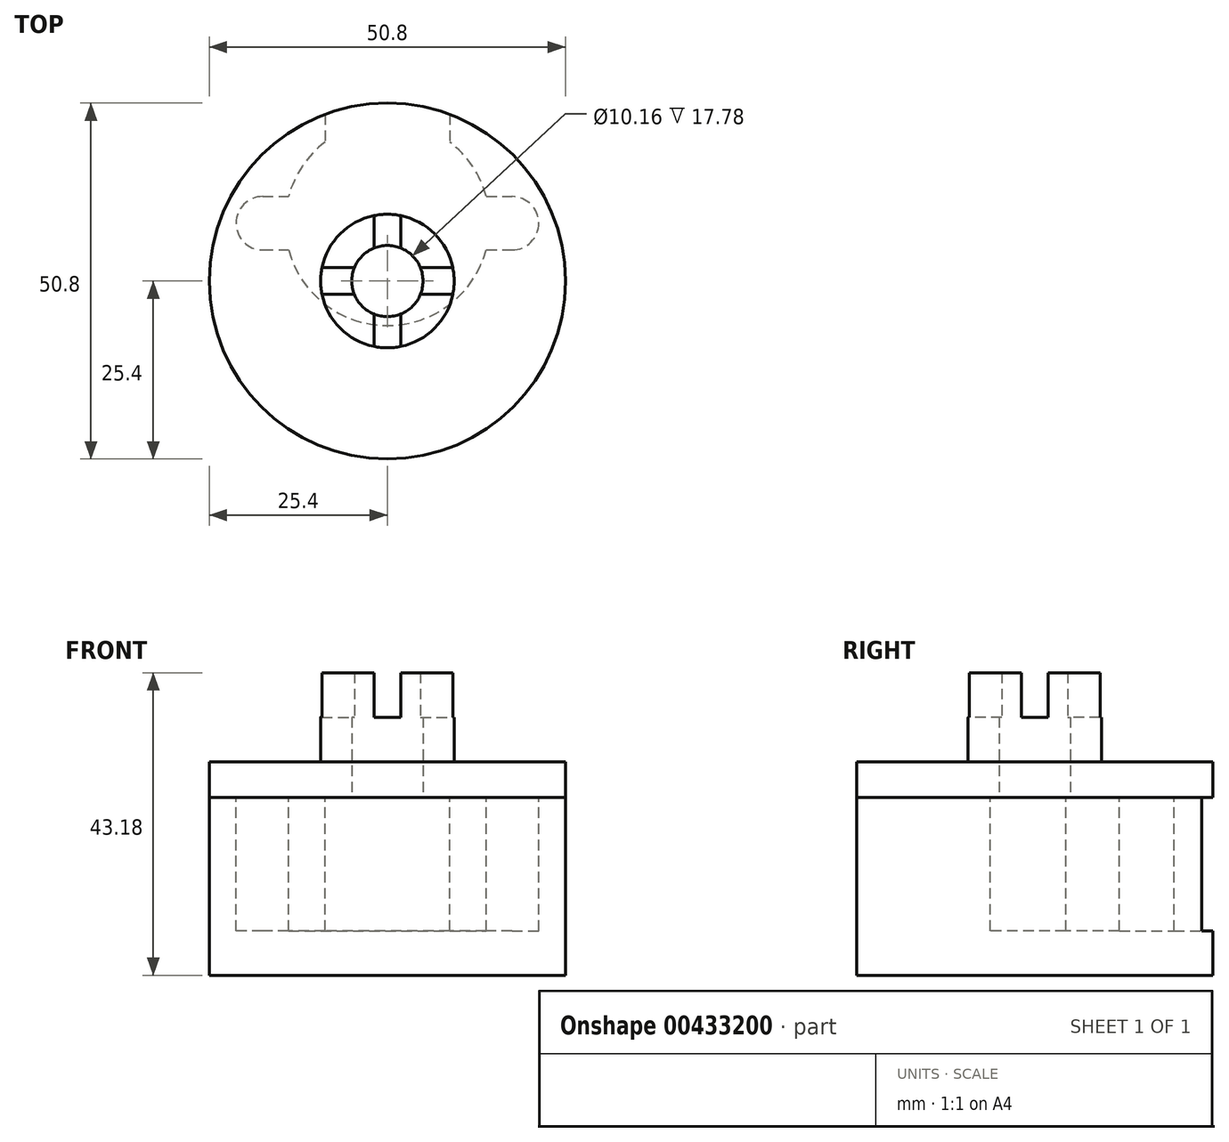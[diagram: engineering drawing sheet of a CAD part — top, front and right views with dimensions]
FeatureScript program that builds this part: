
annotation { "Feature Type Name" : "Feature", "Feature Type Description" : "" }
export const myFeature = defineFeature(function(context is Context, id is Id, definition is map)
    precondition{}
    {
        {
            var Q0;
            Q0=qCreatedBy(makeId("Top.planeOp"),FACE);
            var sketch = newSketch(context, id + "F0", { "sketchPlane" : qUnion([Q0])});
            skCircle(sketch, "E0", {"center": v(0, 0) * mm, "radius": 25.4 * mm});
            skSolve(sketch);
        }
        {
            var Q0;
            Q0=qSketchRegion(id+"F0",true);
            extrude(context, id + "F1", {"entities" : qUnion([Q0]), "depth" : 25.4 * mm});
        }
        {
            var Q0;
            Q0=makeQuery(id+"F1.opExtrude","CAP_FACE",FACE,{"disambiguationData":[OSD([sQuery(id+"F0.wireOp",EDGE,"E0")])],"isStart":false});
            var sketch = newSketch(context, id + "F2", { "sketchPlane" : qUnion([Q0])});
            skCircle(sketch, "E1", {"center": v(0, 8.26) * mm, "radius": 14.6 * mm});
            skSolve(sketch);
        }
        {
            var Q0;
            Q0=qSketchRegion(id+"F2",true);
            extrude(context, id + "F3", {"entities" : qUnion([Q0]), "operationType" : NewBodyOperationType.REMOVE, "oppositeDirection" : true, "depth" : 19.05 * mm});
        }
        {
            var Q0;
            Q0=qCreatedBy(makeId("Front.planeOp"),FACE);
            var sketch = newSketch(context, id + "F4", { "sketchPlane" : qUnion([Q0])});
            skLineSegment(sketch, "E2.bottom", {"start": v(3.81, 25.4) * mm, "end": v(-3.81, 25.4) * mm});
            skLineSegment(sketch, "E2.top", {"start": v(3.81, 21.6) * mm, "end": v(-3.81, 21.6) * mm});
            skLineSegment(sketch, "E2.left", {"start": v(3.8, 25.4) * mm, "end": v(3.8, 21.6) * mm});
            skLineSegment(sketch, "E2.right", {"start": v(-3.81, 25.4) * mm, "end": v(-3.81, 21.6) * mm});
            skPoint(sketch, "E3", {"position": v(0, 21.6) * mm});
            skPoint(sketch, "E4", {"position": v(0, 0) * mm});
            skSolve(sketch);
        }
        {
            var Q0;
            Q0=qSketchRegion(id+"F4",true);
            extrude(context, id + "F5", {"entities" : qUnion([Q0]), "operationType" : NewBodyOperationType.REMOVE, "endBound" : BoundingType.THROUGH_ALL, "oppositeDirection" : true, "depth" : 25.4 * mm});
        }
        {
            var Q0;
            Q0=makeQuery(id+"F1.opExtrude","CAP_FACE",FACE,{"disambiguationData":[OSD([sQuery(id+"F0.wireOp",EDGE,"E0")])],"isStart":true});
            var sketch = newSketch(context, id + "F6", { "sketchPlane" : qUnion([Q0])});
            skCircle(sketch, "E5", {"center": v(0, 0) * mm, "radius": 26.67 * mm});
            skCircle(sketch, "E6", {"center": v(0, 0) * mm, "radius": 39.37 * mm});
            skSolve(sketch);
        }
        {
            var Q0;
            {var subQ0=sQuery(id+"F0.wireOp",EDGE,"E0");Q0=makeQuery(id+"FJPV0hFGGrhg0R9_1.boolean.opBoolean","SPLIT",FACE,{"disambiguationData":[TD([makeQuery(id+"FJPV0hFGGrhg0R9_1.opExtrude","SWEPT_FACE",FACE,{"disambiguationData":[OSD([sQuery(id+"FcM5QLI4IMBpVGz_1.wireOp",EDGE,"NRbNdp12-4AAS-j3ul-Si8F-1Q8l9uEgGX0d")])]})])],"derivedFrom":makeQuery(id+"F1.opExtrude","CAP_FACE",FACE,{"disambiguationData":[OSD([subQ0])],"isStart":false})});}
            var sketch = newSketch(context, id + "F7", { "sketchPlane" : qUnion([Q0])});
            skLineSegment(sketch, "E7.bottom", {"start": v(-8.9, 26.67) * mm, "end": v(8.9, 26.67) * mm});
            skLineSegment(sketch, "E7.top", {"start": v(-8.9, 19.84) * mm, "end": v(8.9, 19.84) * mm});
            skLineSegment(sketch, "E7.left", {"start": v(-8.9, 26.67) * mm, "end": v(-8.9, 19.84) * mm});
            skLineSegment(sketch, "E7.right", {"start": v(8.89, 26.67) * mm, "end": v(8.89, 19.84) * mm});
            skPoint(sketch, "E8", {"position": v(0, -6.35) * mm});
            skSolve(sketch);
        }
        {
            var Q0;
            Q0=qSketchRegion(id+"F7",true);
            var Q1;
            Q1=makeQuery(id+"F3.boolean.opBoolean","COPY",FACE,{"derivedFrom":makeQuery(id+"F3.opExtrude","CAP_FACE",FACE,{"disambiguationData":[OSD([sQuery(id+"F2.wireOp",EDGE,"E1")])],"isStart":false})});
            extrude(context, id + "F8", {"entities" : qUnion([Q0]), "operationType" : NewBodyOperationType.REMOVE, "endBound" : BoundingType.UP_TO_SURFACE, "oppositeDirection" : true, "depth" : 25.4 * mm, "endBoundEntityFace" : qUnion([Q1]), "offsetDistance" : 25.4 * mm});
        }
        {
            var Q0;
            {var subQ0=sQuery(id+"F0.wireOp",EDGE,"E0");Q0=makeQuery(id+"FJPV0hFGGrhg0R9_1.boolean.opBoolean","SPLIT",FACE,{"disambiguationData":[TD([makeQuery(id+"FJPV0hFGGrhg0R9_1.opExtrude","SWEPT_FACE",FACE,{"disambiguationData":[OSD([sQuery(id+"FcM5QLI4IMBpVGz_1.wireOp",EDGE,"NRbNdp12-4AAS-j3ul-Si8F-1Q8l9uEgGX0d")])]})])],"derivedFrom":makeQuery(id+"F1.opExtrude","CAP_FACE",FACE,{"disambiguationData":[OSD([subQ0])],"isStart":false})});}
            var sketch = newSketch(context, id + "F9", { "sketchPlane" : qUnion([Q0])});
            skLineSegment(sketch, "E9", {"start": v(-17.78, 12.07) * mm, "end": v(17.78, 12.07) * mm});
            skLineSegment(sketch, "E10", {"start": v(-17.78, 4.45) * mm, "end": v(17.78, 4.45) * mm});
            skArc(sketch, "E11", {"start": v(-17.78, 12.06) * mm, "mid": v(-21.6, 8.25) * mm, "end": v(-17.78, 4.44) * mm});
            skArc(sketch, "E12", {"start": v(17.78, 4.45) * mm, "mid": v(21.6, 8.26) * mm, "end": v(17.78, 12.07) * mm});
            skLineSegment(sketch, "E13", {"start": v(-17.78, 8.26) * mm, "end": v(17.78, 8.26) * mm, "construction": true});
            skPoint(sketch, "E14", {"position": v(-21.6, 8.25) * mm});
            skPoint(sketch, "E15", {"position": v(21.6, 8.26) * mm});
            skPoint(sketch, "E16", {"position": v(0, 8.26) * mm});
            skSolve(sketch);
        }
        {
            var Q0;
            Q0=qSketchRegion(id+"F9",true);
            var Q1;
            {var subQ0=sQuery(id+"F2.wireOp",EDGE,"E1");Q1=makeQuery(id+"F8.boolean.opBoolean","MERGE",FACE,{"derivedFrom":[makeQuery(id+"F3.boolean.opBoolean","COPY",FACE,{"derivedFrom":makeQuery(id+"F3.opExtrude","CAP_FACE",FACE,{"disambiguationData":[OSD([subQ0])],"isStart":false})}),makeQuery(id+"F8.opExtrude","CAP_FACE",FACE,{"disambiguationData":[OSD([subQ0])],"isStart":false})]});}
            extrude(context, id + "F10", {"entities" : qUnion([Q0]), "operationType" : NewBodyOperationType.REMOVE, "endBound" : BoundingType.UP_TO_SURFACE, "oppositeDirection" : true, "depth" : 25.4 * mm, "endBoundEntityFace" : qUnion([Q1]), "offsetDistance" : 25.4 * mm});
        }
        {
            var Q0;
            Q0=makeQuery(id+"F1.opExtrude","CAP_FACE",FACE,{"disambiguationData":[OSD([sQuery(id+"F0.wireOp",EDGE,"E0")])],"isStart":false});
            var sketch = newSketch(context, id + "F11", { "sketchPlane" : qUnion([Q0])});
            skCircle(sketch, "E17", {"center": v(0, 0) * mm, "radius": 25.4 * mm});
            skCircle(sketch, "E18", {"center": v(0, 0) * mm, "radius": 5.08 * mm});
            skSolve(sketch);
        }
        {
            var Q0;
            Q0 = qSketchRegion(id + "F11", true);
            extrude(context, id + "F12", {"entities" : qUnion([Q0]), "depth" : 5.08 * mm, "offsetDistance" : 25.4 * mm});
        }
        {
            var Q0;
            Q0=makeQuery(id+"F12.opExtrude","CAP_FACE",FACE,{"disambiguationData":[OSD([sQuery(id+"F11.wireOp",EDGE,"E17"),sQuery(id+"F11.wireOp",EDGE,"E18")])],"isStart":false});
            var sketch = newSketch(context, id + "F13", { "sketchPlane" : qUnion([Q0])});
            skCircle(sketch, "E19", {"center": v(0, 0) * mm, "radius": 9.53 * mm});
            skCircle(sketch, "E20", {"center": v(0, 0) * mm, "radius": 5.08 * mm});
            skSolve(sketch);
        }
        {
            var Q0;
            Q0 = qSketchRegion(id + "F13", true);
            extrude(context, id + "F14", {"entities" : qUnion([Q0]), "operationType" : NewBodyOperationType.ADD, "depth" : 12.7 * mm, "offsetDistance" : 25.4 * mm});
        }
        {
            var Q0;
            Q0=makeQuery(id+"F14.opExtrude","CAP_FACE",FACE,{"disambiguationData":[OSD([sQuery(id+"F13.wireOp",EDGE,"E19"),sQuery(id+"F13.wireOp",EDGE,"E20")])],"isStart":false});
            var sketch = newSketch(context, id + "F15", { "sketchPlane" : qUnion([Q0])});
            skLineSegment(sketch, "E21.bottom", {"start": v(-1.9, 14.6) * mm, "end": v(1.9, 14.6) * mm});
            skLineSegment(sketch, "E21.top", {"start": v(-1.9, -14.6) * mm, "end": v(1.9, -14.6) * mm});
            skLineSegment(sketch, "E21.left", {"start": v(-1.9, 14.6) * mm, "end": v(-1.9, 1.9) * mm});
            skLineSegment(sketch, "E21.right", {"start": v(1.9, 14.6) * mm, "end": v(1.9, 1.9) * mm});
            skPoint(sketch, "E21.middle", {"position": v(0, 0) * mm});
            skLineSegment(sketch, "E22.bottom", {"start": v(-14.6, 1.9) * mm, "end": v(-1.9, 1.9) * mm});
            skLineSegment(sketch, "E22.top", {"start": v(-14.6, -1.9) * mm, "end": v(-1.9, -1.9) * mm});
            skLineSegment(sketch, "E22.left", {"start": v(-14.6, 1.9) * mm, "end": v(-14.6, -1.9) * mm});
            skLineSegment(sketch, "E22.right", {"start": v(14.6, 1.9) * mm, "end": v(14.6, -1.9) * mm});
            skLineSegment(sketch, "E23.trimOffspring", {"start": v(1.9, 1.9) * mm, "end": v(14.6, 1.9) * mm});
            skLineSegment(sketch, "E24.trimOffspring", {"start": v(1.9, -1.9) * mm, "end": v(1.9, -14.6) * mm});
            skLineSegment(sketch, "E25.trimOffspring", {"start": v(1.9, -1.9) * mm, "end": v(14.6, -1.9) * mm});
            skLineSegment(sketch, "E26.trimOffspring", {"start": v(-1.9, -1.9) * mm, "end": v(-1.9, -14.6) * mm});
            skSolve(sketch);
        }
        {
            var Q0;
            Q0 = qSketchRegion(id + "F15", true);
            extrude(context, id + "F16", {"entities" : qUnion([Q0]), "operationType" : NewBodyOperationType.REMOVE, "oppositeDirection" : true, "depth" : 6.35 * mm, "offsetDistance" : 25.4 * mm});
        }
    });
